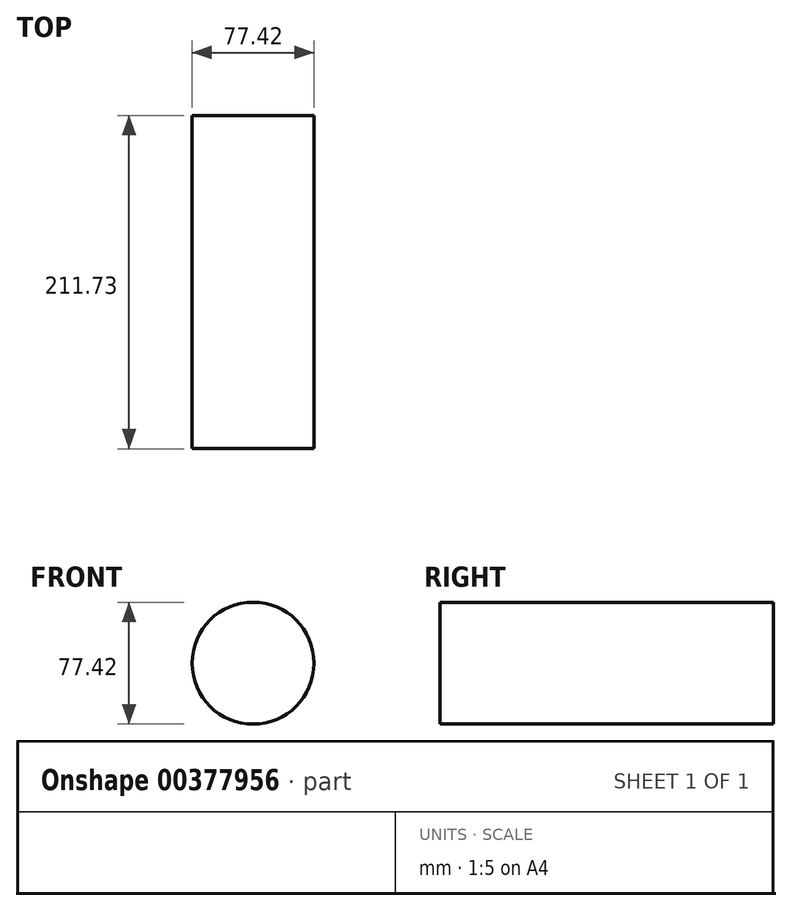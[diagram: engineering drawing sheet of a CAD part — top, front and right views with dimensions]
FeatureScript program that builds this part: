
annotation { "Feature Type Name" : "Feature", "Feature Type Description" : "" }
export const myFeature = defineFeature(function(context is Context, id is Id, definition is map)
    precondition{}
    {
        {
            var Q0;
            Q0=qCreatedBy(makeId("Front.planeOp"),FACE);
            var sketch = newSketch(context, id + "F0", { "sketchPlane" : qUnion([Q0])});
            skCircle(sketch, "E0", {"center": v(0, 0) * mm, "radius": 38.7 * mm});
            skSolve(sketch);
        }
        {
            var Q0;
            Q0=makeQuery(id+"F0.imprint","IMPRINT",FACE,{"disambiguationData":[TD([[makeQuery(id+"F0.imprint","IMPRINT",EDGE,{"derivedFrom":sQuery(id+"F0.wireOp",EDGE,"E0")}),1.0]])]});
            extrude(context, id + "F1", {"entities" : qUnion([Q0]), "depth" : 211.73 * mm});
        }
    });
